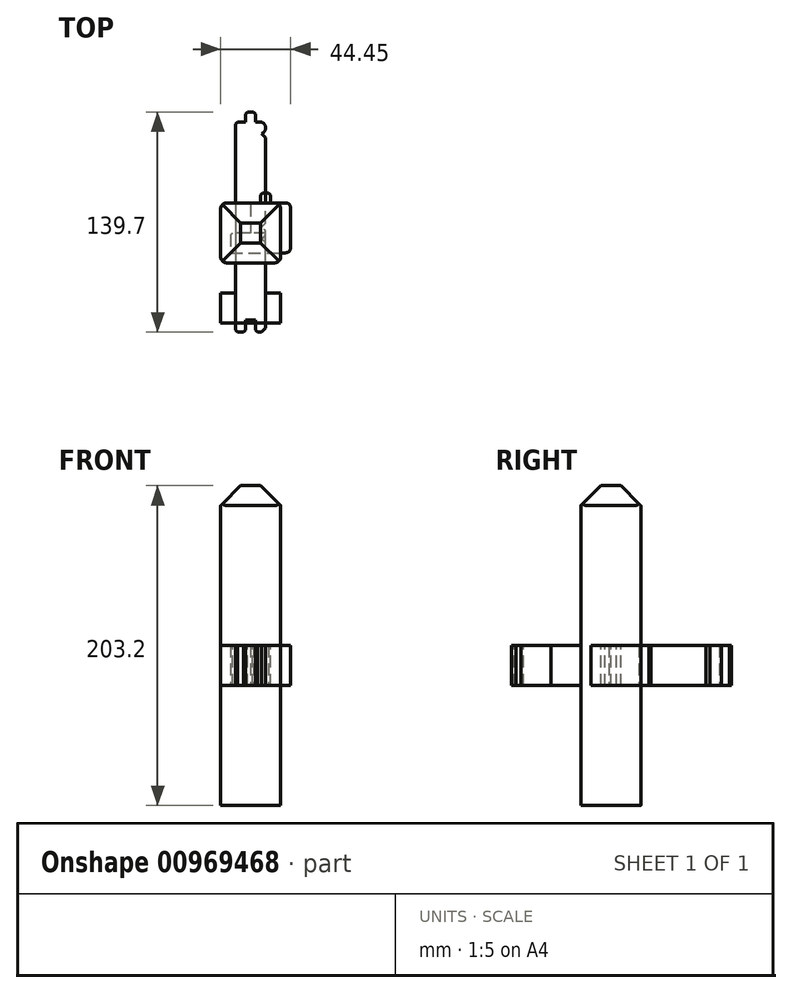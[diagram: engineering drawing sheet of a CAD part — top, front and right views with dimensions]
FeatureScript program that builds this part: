
annotation { "Feature Type Name" : "Feature", "Feature Type Description" : "" }
export const myFeature = defineFeature(function(context is Context, id is Id, definition is map)
    precondition{}
    {
        {
            var Q0;
            Q0=qCreatedBy(makeId("Top.planeOp"),FACE);
            var sketch = newSketch(context, id + "F0", { "sketchPlane" : qUnion([Q0])});
            skLineSegment(sketch, "E0", {"start": v(-3.18, -55.41) * mm, "end": v(3.17, -55.41) * mm});
            skLineSegment(sketch, "E1", {"start": v(3.18, -55.41) * mm, "end": v(3.18, -63.03) * mm});
            skLineSegment(sketch, "E2", {"start": v(3.17, -63.03) * mm, "end": v(6.83, -63.03) * mm});
            skLineSegment(sketch, "E3", {"start": v(9.52, -60.34) * mm, "end": v(9.52, -6.34) * mm});
            skLineSegment(sketch, "E4", {"start": v(9.53, -6.34) * mm, "end": v(6.83, -3.64) * mm});
            skLineSegment(sketch, "E5", {"start": v(6.83, 3.64) * mm, "end": v(9.53, 6.34) * mm});
            skLineSegment(sketch, "E6", {"start": v(9.52, 6.34) * mm, "end": v(9.52, 60.34) * mm});
            skLineSegment(sketch, "E7", {"start": v(6.83, 63.03) * mm, "end": v(9.52, 60.34) * mm});
            skLineSegment(sketch, "E8", {"start": v(6.83, 70.32) * mm, "end": v(3.17, 70.32) * mm});
            skLineSegment(sketch, "E9", {"start": v(3.17, 70.32) * mm, "end": v(3.17, 76.67) * mm});
            skLineSegment(sketch, "E10", {"start": v(3.17, 76.67) * mm, "end": v(-3.18, 76.67) * mm});
            skLineSegment(sketch, "E11", {"start": v(-3.17, 76.67) * mm, "end": v(-3.17, 70.32) * mm});
            skLineSegment(sketch, "E12", {"start": v(-3.18, 70.32) * mm, "end": v(-9.52, 70.32) * mm});
            skLineSegment(sketch, "E13", {"start": v(-9.53, 70.32) * mm, "end": v(-9.52, -63.03) * mm});
            skLineSegment(sketch, "E14", {"start": v(-9.53, -63.03) * mm, "end": v(-3.18, -63.03) * mm});
            skLineSegment(sketch, "E15", {"start": v(-3.17, -63.03) * mm, "end": v(-3.17, -55.41) * mm});
            skLineSegment(sketch, "E16", {"start": v(6.83, -63.03) * mm, "end": v(9.52, -60.34) * mm});
            skArc(sketch, "E17", {"start": v(6.83, -3.64) * mm, "mid": v(9.53, 0) * mm, "end": v(6.83, 3.64) * mm});
            skArc(sketch, "E18", {"start": v(6.83, 63.03) * mm, "mid": v(9.53, 66.67) * mm, "end": v(6.83, 70.32) * mm});
            skSolve(sketch);
        }
        {
            var Q0;
            Q0 = qSketchRegion(id + "F0", true);
            extrude(context, id + "F1", {"entities" : qUnion([Q0]), "oppositeDirection" : true, "depth" : 25.4 * mm, "offsetDistance" : 25.4 * mm});
        }
        {
            var Q0;
            Q0=makeQuery(id+"F1.opExtrude","SWEPT_EDGE",EDGE,{"disambiguationData":[OSD([sQuery(id+"F0.wireOp",EDGE,"E10"),sQuery(id+"F0.wireOp",EDGE,"E11")])]});
            var Q1;
            Q1=makeQuery(id+"F1.opExtrude","SWEPT_EDGE",EDGE,{"disambiguationData":[OSD([sQuery(id+"F0.wireOp",EDGE,"E12"),sQuery(id+"F0.wireOp",EDGE,"E13")])]});
            var Q2;
            Q2=makeQuery(id+"F1.opExtrude","SWEPT_EDGE",EDGE,{"disambiguationData":[OSD([sQuery(id+"F0.wireOp",EDGE,"E9"),sQuery(id+"F0.wireOp",EDGE,"E10")])]});
            var Q3;
            Q3=makeQuery(id+"F1.opExtrude","SWEPT_EDGE",EDGE,{"disambiguationData":[OSD([sQuery(id+"F0.wireOp",EDGE,"E13"),sQuery(id+"F0.wireOp",EDGE,"E14")])]});
            var Q4;
            Q4=makeQuery(id+"F1.opExtrude","SWEPT_EDGE",EDGE,{"disambiguationData":[OSD([sQuery(id+"F0.wireOp",EDGE,"E14"),sQuery(id+"F0.wireOp",EDGE,"E15")])]});
            var Q5;
            Q5=makeQuery(id+"F1.opExtrude","SWEPT_EDGE",EDGE,{"disambiguationData":[OSD([sQuery(id+"F0.wireOp",EDGE,"E1"),sQuery(id+"F0.wireOp",EDGE,"E2")])]});
            chamfer(context, id + "F2", {"entities" : qUnion([Q0, Q1, Q2, Q3, Q4, Q5]), "width" : 1.27 * mm, "tangentPropagation" : true});
        }
        {
            var Q0;
            Q0=qCreatedBy(makeId("Top.planeOp"),FACE);
            var sketch = newSketch(context, id + "F3", { "sketchPlane" : qUnion([Q0])});
            skLineSegment(sketch, "E19", {"start": v(0, 0) * mm, "end": v(-12.7, 0) * mm});
            skLineSegment(sketch, "E20", {"start": v(-12.7, 0) * mm, "end": v(-12.7, -12.7) * mm});
            skLineSegment(sketch, "E21", {"start": v(-12.7, -12.7) * mm, "end": v(25.4, -12.7) * mm});
            skLineSegment(sketch, "E22", {"start": v(25.4, -12.7) * mm, "end": v(25.4, 19.05) * mm});
            skLineSegment(sketch, "E23", {"start": v(25.4, 19.05) * mm, "end": v(12.7, 19.05) * mm});
            skLineSegment(sketch, "E24", {"start": v(12.7, 19.05) * mm, "end": v(12.7, 25.4) * mm});
            skLineSegment(sketch, "E25", {"start": v(12.7, 25.4) * mm, "end": v(6.35, 25.4) * mm});
            skLineSegment(sketch, "E26", {"start": v(6.35, 25.4) * mm, "end": v(6.35, 19.05) * mm});
            skLineSegment(sketch, "E27", {"start": v(6.35, 19.05) * mm, "end": v(0, 19.05) * mm});
            skLineSegment(sketch, "E28", {"start": v(0, 19.05) * mm, "end": v(0, 0) * mm});
            skSolve(sketch);
        }
        {
            var Q0;
            Q0=makeQuery(id+"F3.imprint","IMPRINT",FACE,{"disambiguationData":[TD([[makeQuery(id+"F3.imprint","IMPRINT",EDGE,{"derivedFrom":sQuery(id+"F3.wireOp",EDGE,"E19")}),1.0]])]});
            extrude(context, id + "F4", {"entities" : qUnion([Q0]), "oppositeDirection" : true, "depth" : 25.4 * mm, "offsetDistance" : 25.4 * mm});
        }
        {
            var Q0;
            Q0=makeQuery(id+"F4.opExtrude","SWEPT_EDGE",EDGE,{"disambiguationData":[OSD([sQuery(id+"F3.wireOp",EDGE,"E24"),sQuery(id+"F3.wireOp",EDGE,"E25")])]});
            var Q1;
            Q1=makeQuery(id+"F4.opExtrude","SWEPT_EDGE",EDGE,{"disambiguationData":[OSD([sQuery(id+"F3.wireOp",EDGE,"E25"),sQuery(id+"F3.wireOp",EDGE,"E26")])]});
            var Q2;
            Q2=makeQuery(id+"F4.opExtrude","SWEPT_EDGE",EDGE,{"disambiguationData":[OSD([sQuery(id+"F3.wireOp",EDGE,"E27"),sQuery(id+"F3.wireOp",EDGE,"E28")])]});
            var Q3;
            Q3=makeQuery(id+"F4.opExtrude","SWEPT_EDGE",EDGE,{"disambiguationData":[OSD([sQuery(id+"F3.wireOp",EDGE,"E19"),sQuery(id+"F3.wireOp",EDGE,"E20")])]});
            chamfer(context, id + "F5", {"entities" : qUnion([Q0, Q1, Q2, Q3]), "width" : 1.27 * mm, "tangentPropagation" : true});
        }
        {
            var Q0;
            Q0=makeQuery(id+"F4.opExtrude","SWEPT_EDGE",EDGE,{"disambiguationData":[OSD([sQuery(id+"F3.wireOp",EDGE,"E22"),sQuery(id+"F3.wireOp",EDGE,"E23")])]});
            var Q1;
            Q1=makeQuery(id+"F4.opExtrude","SWEPT_EDGE",EDGE,{"disambiguationData":[OSD([sQuery(id+"F3.wireOp",EDGE,"E21"),sQuery(id+"F3.wireOp",EDGE,"E22")])]});
            fillet(context, id + "F6", {"entities" : qUnion([Q0, Q1]), "radius" : 3.17 * mm, "tangentPropagation" : true, "allowEdgeOverflow" : false});
        }
        {
            var Q0;
            Q0=qCreatedBy(makeId("Top.planeOp"),FACE);
            var sketch = newSketch(context, id + "F7", { "sketchPlane" : qUnion([Q0])});
            skLineSegment(sketch, "E29.bottom", {"start": v(19.05, -19.05) * mm, "end": v(-19.05, -19.05) * mm});
            skLineSegment(sketch, "E29.top", {"start": v(19.05, 19.05) * mm, "end": v(-19.05, 19.05) * mm});
            skLineSegment(sketch, "E29.left", {"start": v(19.05, -19.05) * mm, "end": v(19.05, 19.05) * mm});
            skLineSegment(sketch, "E29.right", {"start": v(-19.05, -19.05) * mm, "end": v(-19.05, 19.05) * mm});
            skPoint(sketch, "E29.middle", {"position": v(0, 0) * mm});
            skSolve(sketch);
        }
        {
            var Q0;
            Q0=makeQuery(id+"F7.imprint","IMPRINT",FACE,{"disambiguationData":[TD([[makeQuery(id+"F7.imprint","IMPRINT",EDGE,{"derivedFrom":sQuery(id+"F7.wireOp",EDGE,"E29.bottom")}),-1.0]])]});
            extrude(context, id + "F8", {"entities" : qUnion([Q0]), "endBound" : BoundingType.SYMMETRIC, "oppositeDirection" : true, "depth" : 203.2 * mm, "offsetDistance" : 25.4 * mm});
        }
        {
            var Q0;
            Q0=makeQuery(id+"F8.opExtrude","SWEPT_EDGE",EDGE,{"disambiguationData":[OSD([sQuery(id+"F7.wireOp",EDGE,"E29.bottom"),sQuery(id+"F7.wireOp",EDGE,"E29.right")])]});
            var Q1;
            Q1=makeQuery(id+"F8.opExtrude","SWEPT_EDGE",EDGE,{"disambiguationData":[OSD([sQuery(id+"F7.wireOp",EDGE,"E29.bottom"),sQuery(id+"F7.wireOp",EDGE,"E29.left")])]});
            var Q2;
            Q2=makeQuery(id+"F8.opExtrude","SWEPT_EDGE",EDGE,{"disambiguationData":[OSD([sQuery(id+"F7.wireOp",EDGE,"E29.top"),sQuery(id+"F7.wireOp",EDGE,"E29.left")])]});
            var Q3;
            Q3=makeQuery(id+"F8.opExtrude","SWEPT_EDGE",EDGE,{"disambiguationData":[OSD([sQuery(id+"F7.wireOp",EDGE,"E29.top"),sQuery(id+"F7.wireOp",EDGE,"E29.right")])]});
            fillet(context, id + "F9", {"entities" : qUnion([Q0, Q1, Q2, Q3]), "radius" : 3.8 * mm, "tangentPropagation" : true, "allowEdgeOverflow" : false});
        }
        {
            var Q0;
            Q0=makeQuery(id+"F8.opExtrude","CAP_EDGE",EDGE,{"disambiguationData":[OSD([sQuery(id+"F7.wireOp",EDGE,"E29.top")])],"isStart":true});
            var Q1;
            Q1=makeQuery(id+"F8.opExtrude","CAP_EDGE",EDGE,{"disambiguationData":[OSD([sQuery(id+"F7.wireOp",EDGE,"E29.right")])],"isStart":true});
            var Q2;
            Q2=makeQuery(id+"F8.opExtrude","CAP_EDGE",EDGE,{"disambiguationData":[OSD([sQuery(id+"F7.wireOp",EDGE,"E29.bottom")])],"isStart":true});
            var Q3;
            Q3=makeQuery(id+"F8.opExtrude","CAP_EDGE",EDGE,{"disambiguationData":[OSD([sQuery(id+"F7.wireOp",EDGE,"E29.left")])],"isStart":true});
            chamfer(context, id + "F10", {"entities" : qUnion([Q0, Q1, Q2, Q3]), "width" : 12.7 * mm});
        }
        {
            var Q0;
            Q0=qCreatedBy(makeId("Top.planeOp"),FACE);
            var sketch = newSketch(context, id + "F11", { "sketchPlane" : qUnion([Q0])});
            skLineSegment(sketch, "E30", {"start": v(19.05, -38.1) * mm, "end": v(9.52, -38.1) * mm});
            skLineSegment(sketch, "E31", {"start": v(9.53, -38.1) * mm, "end": v(9.53, 0) * mm});
            skLineSegment(sketch, "E32", {"start": v(9.52, 0) * mm, "end": v(-9.53, 0) * mm});
            skLineSegment(sketch, "E33", {"start": v(-9.53, 0) * mm, "end": v(-9.52, -38.1) * mm});
            skLineSegment(sketch, "E34", {"start": v(-9.52, -38.1) * mm, "end": v(-19.05, -38.1) * mm});
            skLineSegment(sketch, "E35", {"start": v(-19.05, -38.1) * mm, "end": v(-19.05, -57.15) * mm});
            skLineSegment(sketch, "E36", {"start": v(-19.05, -57.15) * mm, "end": v(19.05, -57.15) * mm});
            skLineSegment(sketch, "E37", {"start": v(19.05, -57.15) * mm, "end": v(19.05, -38.1) * mm});
            skSolve(sketch);
        }
        {
            var Q0;
            Q0=makeQuery(id+"F11.imprint","IMPRINT",FACE,{"disambiguationData":[TD([[makeQuery(id+"F11.imprint","IMPRINT",EDGE,{"derivedFrom":sQuery(id+"F11.wireOp",EDGE,"E30")}),1.0]])]});
            extrude(context, id + "F12", {"entities" : qUnion([Q0]), "oppositeDirection" : true, "depth" : 25.4 * mm, "offsetDistance" : 25.4 * mm});
        }
    });
